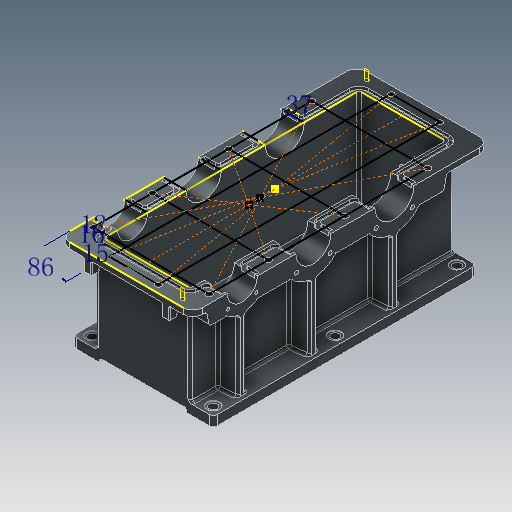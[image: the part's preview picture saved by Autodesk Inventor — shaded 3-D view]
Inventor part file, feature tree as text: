
AUTODESK INVENTOR PART (.ipt)
format: ipt  version: 2025 (Build 290162000, 162)  size: 1,593,856 bytes
history: native  units: mm
features: sketch x24, reference x17, other x15, extrude x14, hole x8, fillet x5, plane x5, revolve x4, projected_geometry x4, mirror x3, thread x2
ambient origin geometry x8: Origin, YZ Plane, XZ Plane, XY Plane, X Axis, Y Axis, Z Axis, Center Point
bodies: Body1 (feature_tree)
feature tree (101):
  other  "箱体底部"
  extrude  "拉伸1"  Depth=540.0mm
  extrude  "拉伸2"  Depth=194.0mm
  extrude  "拉伸3"  Depth=8.0mm
  extrude  "拉伸4"  Depth=42.0mm
  extrude  "拉伸5"  Depth=62.0mm
  extrude  "拉伸6"  Depth=72.0mm
  fillet  "圆角7"  Radius=80.0mm
  hole  "孔1"  [1 undecoded]
  sketch  "草图8"  dims[d25=6.0mm d26=6.0mm]
  hole  "孔2"  [1 undecoded]
  hole  "孔3"  [1 undecoded]
  extrude  "拉伸7"  Depth=36.0mm
  mirror  "镜像1"
  other  "加强筋1"
  mirror  "镜像2"
  mirror  "镜像3"
  hole  "孔4"  [1 undecoded]
  revolve  "旋转1"  [1 undecoded]
  revolve  "旋转2"  [1 undecoded]
  extrude  "拉伸8"  Depth=8.0mm
  thread  "螺纹1"  [1 undecoded]
  plane  "工作平面1"
  extrude  "拉伸9"  Depth=8.0mm
  fillet  "圆角12"  Radius=11.0mm
  extrude  "拉伸10"  Depth=11.0mm
  thread  "螺纹2"  [1 undecoded]
  extrude  "拉伸11"  Depth=11.0mm
  fillet  "圆角13"  Radius=180.0mm
  fillet  "圆角14"  Radius=8.0mm
  hole  "孔6"  [1 undecoded]
  hole  "孔7"  [1 undecoded]
  hole  "孔8"  [1 undecoded]
  hole  "孔9"  [1 undecoded]
  plane  "工作平面2"
  plane  "工作平面3"
  sketch  "草图25"  dims[d70=86.0mm d73=12.0mm]
  extrude  "拉伸12"  Depth=2.0mm
  extrude  "拉伸13"  Depth=2.0mm
  extrude  "拉伸15"  Depth=2.0mm
  plane  "工作平面4"
  revolve  "旋转3"  [1 undecoded]
  plane  "工作平面5"
  revolve  "旋转4"  [1 undecoded]
  fillet  "圆角15"  Radius=40.0mm
  sketch  "草图1"  dims[d0=288.0mm d1=540.0mm]
  sketch  "草图2"  dims[d2=20.0mm d3=0.0mm d4=194.0mm]
  sketch  "草图3"  dims[d5=197.0mm d6=0.0mm d8=8.0mm]
  sketch  "草图4"  dims[d10=47.0mm d11=42.0mm]
  sketch  "草图5"  dims[d12=12.0mm d13=0.0mm d15=62.0mm]
  sketch  "草图6"  dims[d16=0.0mm d17=0.0mm d18=72.0mm d20=80.0mm]
  sketch  "草图7"  dims[d23=20.0mm d24=8.0mm]
  reference  "参考1"
  sketch  "草图11"  dims[d27=8.0mm d28=6.0mm d29=0.0mm]
  projected_geometry  "投影回路1"
  sketch  "草图13"  dims[d31=36.0mm d38=36.0mm]
  projected_geometry  "投影回路2"
  projected_geometry  "投影回路3"
  sketch  "草图14"  dims[d39=36.0mm d40=36.0mm]
  sketch  "草图15"  dims[d41=36.0mm d42=36.0mm]
  sketch  "草图16"  dims[d43=5.0mm d44=8.0mm]
  projected_geometry  "投影回路4"
  sketch  "草图17"  dims[d45=8.0mm d46=8.0mm d47=8.0mm]
  sketch  "草图18"  dims[d48=8.0mm d49=8.0mm d50=11.0mm]
  sketch  "草图19"  dims[d51=11.0mm d52=11.0mm d53=11.0mm]
  sketch  "草图21"  dims[d54=11.0mm d55=11.0mm d56=180.0mm d57=8.0mm d58=0.0mm]
  reference  "参考6"
  reference  "参考7"
  sketch  "草图22"  dims[d59=6.0mm]
  reference  "参考8"
  reference  "参考9"
  sketch  "草图23"  dims[d60=17.0mm d61=6.0mm d62=26.0mm d63=1.5mm d64=90.0deg d65=8.0mm d66=20.594885mm d67=20.0mm]
  reference  "参考10"
  reference  "参考11"
  reference  "参考12"
  reference  "参考13"
  sketch  "草图24"  dims[d68=20.0mm d69=15.0mm]
  reference  "参考14"
  reference  "参考15"
  reference  "参考16"
  reference  "参考17"
  sketch  "草图27"  dims[d74=16.0mm d75=37.0mm]
  sketch  "草图28"  dims[d76=13.0mm d77=6.0mm d78=26.0mm d79=1.5mm d80=90.0deg d81=8.0mm d82=20.594885mm]
  reference  "参考19"
  reference  "参考20"
  sketch  "草图29"  dims[d83=12.0mm d84=6.0mm d85=4.0mm d86=2.0mm d87=90.0deg d88=8.0mm d89=20.594885mm d90=166.25mm d91=146.0mm d92=102.0mm d93=122.0mm d94=130.0mm d95=40.0mm d96=17.715092mm d97=13.700835mm d98=10.0mm d99=130.0mm d100=0.0mm d101=5.0mm d102=16.0mm d103=10.0mm d104=0.872665mm d105=0.0mm d106=1.0mm d107=1.0mm d108=5.0mm d109=13.0mm d110=6.0mm d111=4.0mm d112=2.0mm d113=90.0deg d114=8.0mm d115=20.594885mm d118=15.0mm d120=110.0mm d121=360.0deg d122=15.0mm d123=12.5mm d124=2.0mm d125=6.0mm d126=360.0deg d127=50.0mm d128=0.0mm d129=20.0mm d130=17.0mm d131=6.0mm d132=26.0mm d133=28.0mm d134=50.0mm d135=0.0mm d136=5.0mm d137=16.0mm d138=10.0mm d139=0.0mm d140=20.0mm d141=0.0mm d142=2.5mm d143=10.0mm d144=10.0mm d145=0.0mm d146=2.0mm d147=0.5mm d155=6.647mm d156=28.0mm d157=4.0mm d158=2.0mm d159=90.0deg d160=30.0mm d161=120.0deg d162=6.647mm d163=28.0mm d164=4.0mm d165=2.0mm d166=90.0deg d167=30.0mm d168=120.0deg d169=8.376mm d170=28.0mm d171=4.0mm d172=2.0mm d173=90.0deg d174=30.0mm d175=120.0deg d176=8.376mm d177=28.0mm d178=4.0mm d179=2.0mm d180=90.0deg d181=30.0mm d182=120.0deg d183=80.0mm d184=-80.0mm d185=27.0mm d186=4.5mm d187=8.5mm d188=17.0mm d189=2.0mm d190=16.0mm d191=0.0mm d192=16.0mm d193=0.0mm d196=10.0mm d197=0.0mm d198=90.0deg d199=90.0deg d200=2.0mm d148=0.0mm d149=0.0mm d150=0.0mm]
  reference  "参考21"
  reference  "参考22"
  other  "齿轮箱.iam"
  other  "中间轴:1"
  other  "轴承:2"
  other  "滚动轴承 GB/T 276-1994 60000 和 160000 型 6306:1"
  other  "高速轴承闷盖"
  other  "高速轴承透盖"
  other  "中间轴承闷盖1"
  other  "低速轴承透盖"
  other  "中间轴承闷盖2"
  other  "低速轴承闷盖"
  other  "定位销:1"
  other  "定位销:2"
  other  "<userpath>\Desktop\Inventor files\齿轮箱.iam"
note: 14 required parameter values undecoded (feature->parameter linkage not recoverable at this tier; creation-order binding heuristic only, values carry confidence <= 0.55)